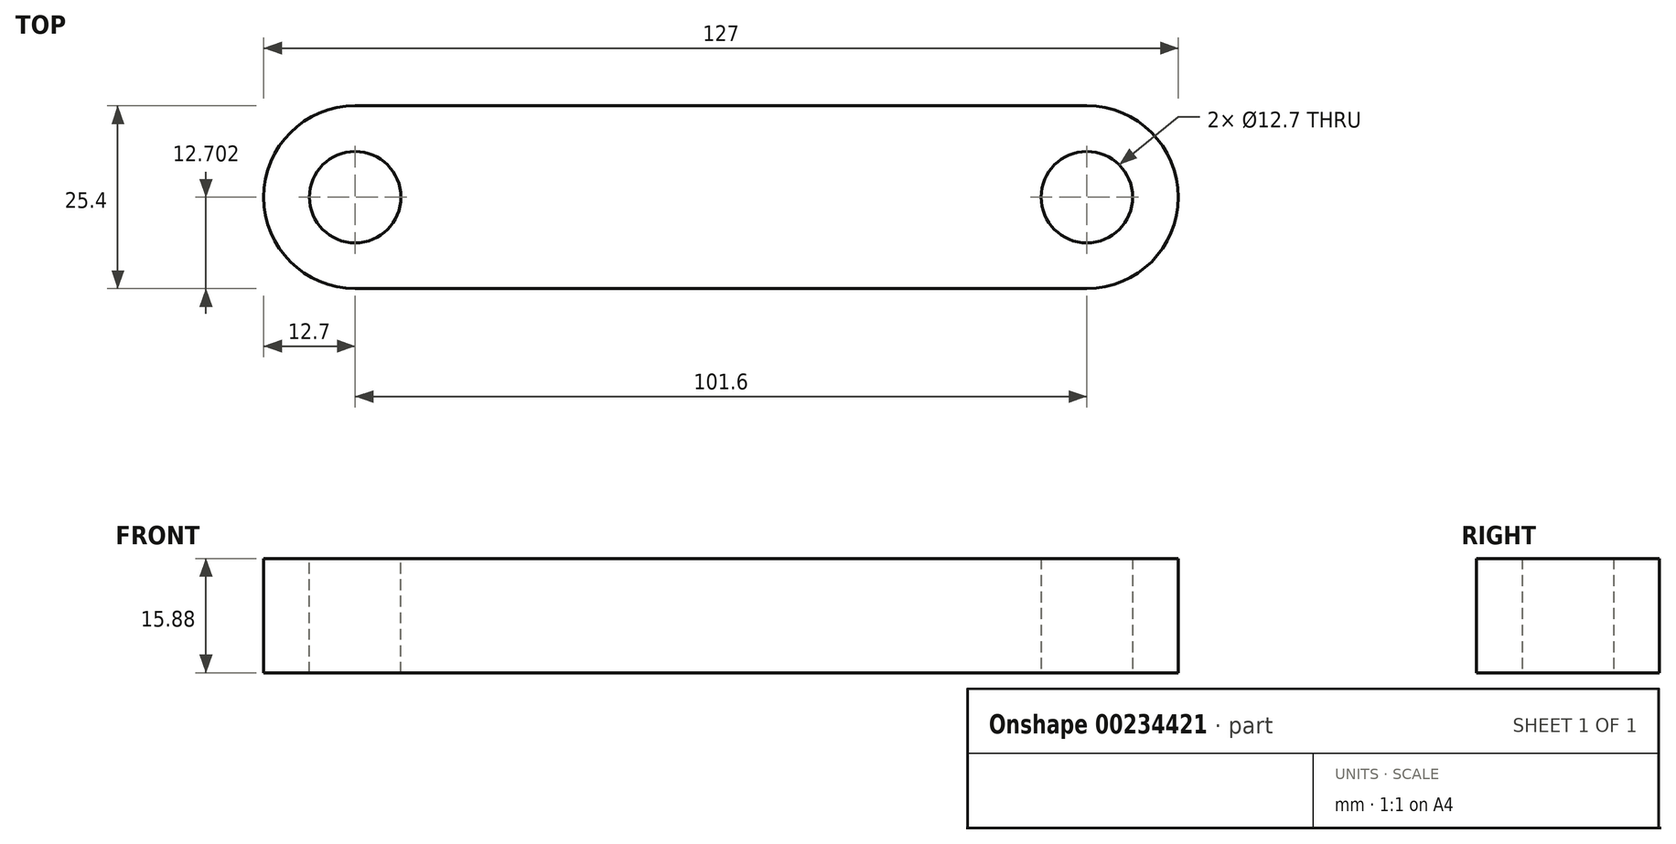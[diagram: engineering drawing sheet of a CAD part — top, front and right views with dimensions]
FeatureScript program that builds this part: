
annotation { "Feature Type Name" : "Feature", "Feature Type Description" : "" }
export const myFeature = defineFeature(function(context is Context, id is Id, definition is map)
    precondition{}
    {
        {
            var Q0;
            Q0=qCreatedBy(makeId("Top.planeOp"),FACE);
            var sketch = newSketch(context, id + "F0", { "sketchPlane" : qUnion([Q0])});
            skLineSegment(sketch, "E0.bottom", {"start": v(1.78, -0.58) * mm, "end": v(128.78, -0.58) * mm});
            skLineSegment(sketch, "E0.top", {"start": v(1.78, 24.82) * mm, "end": v(128.78, 24.82) * mm});
            skLineSegment(sketch, "E0.left", {"start": v(1.78, -0.58) * mm, "end": v(1.78, 24.82) * mm});
            skLineSegment(sketch, "E0.right", {"start": v(128.78, -0.58) * mm, "end": v(128.78, 24.82) * mm});
            skSolve(sketch);
        }
        {
            var Q0;
            Q0=makeQuery(id+"F0.imprint","IMPRINT",FACE,{"disambiguationData":[TD([[makeQuery(id+"F0.imprint","IMPRINT",EDGE,{"derivedFrom":sQuery(id+"F0.wireOp",EDGE,"E0.bottom")}),1.0]])]});
            extrude(context, id + "F1", {"entities" : qUnion([Q0]), "depth" : 15.88 * mm});
        }
        {
            var Q0;
            Q0=makeQuery(id+"F1.opExtrude","CAP_FACE",FACE,{"disambiguationData":[OSD([sQuery(id+"F0.wireOp",EDGE,"E0.bottom"),sQuery(id+"F0.wireOp",EDGE,"E0.top"),sQuery(id+"F0.wireOp",EDGE,"E0.left"),sQuery(id+"F0.wireOp",EDGE,"E0.right")])],"isStart":true});
            var sketch = newSketch(context, id + "F2", { "sketchPlane" : qUnion([Q0])});
            skCircle(sketch, "E1", {"center": v(116.08, -12.12) * mm, "radius": 6.35 * mm});
            skSolve(sketch);
        }
        {
            var Q0;
            Q0=makeQuery(id+"F2.imprint","IMPRINT",FACE,{"disambiguationData":[TD([[makeQuery(id+"F2.imprint","IMPRINT",EDGE,{"derivedFrom":sQuery(id+"F2.wireOp",EDGE,"E1")}),1.0]])]});
            extrude(context, id + "F3", {"entities" : qUnion([Q0]), "operationType" : NewBodyOperationType.REMOVE, "endBound" : BoundingType.THROUGH_ALL, "oppositeDirection" : true, "depth" : 25.4 * mm});
        }
        {
            var Q0;
            Q0=makeQuery(id+"F1.opExtrude","SWEPT_EDGE",EDGE,{"disambiguationData":[OSD([sQuery(id+"F0.wireOp",EDGE,"E0.top"),sQuery(id+"F0.wireOp",EDGE,"E0.right")])]});
            var Q1;
            Q1=makeQuery(id+"F1.opExtrude","SWEPT_EDGE",EDGE,{"disambiguationData":[OSD([sQuery(id+"F0.wireOp",EDGE,"E0.bottom"),sQuery(id+"F0.wireOp",EDGE,"E0.right")])]});
            fillet(context, id + "F4", {"entities" : qUnion([Q0, Q1]), "radius" : 12.7 * mm, "tangentPropagation" : true, "allowEdgeOverflow" : false});
        }
        {
            var Q0;
            Q0=makeQuery(id+"F1.opExtrude","CAP_FACE",FACE,{"disambiguationData":[OSD([sQuery(id+"F0.wireOp",EDGE,"E0.bottom"),sQuery(id+"F0.wireOp",EDGE,"E0.top"),sQuery(id+"F0.wireOp",EDGE,"E0.left"),sQuery(id+"F0.wireOp",EDGE,"E0.right")])],"isStart":false});
            var sketch = newSketch(context, id + "F5", { "sketchPlane" : qUnion([Q0])});
            skCircle(sketch, "E2", {"center": v(14.48, 12.12) * mm, "radius": 6.35 * mm});
            skSolve(sketch);
        }
        {
            var Q0;
            Q0=makeQuery(id+"F5.imprint","IMPRINT",FACE,{"disambiguationData":[TD([[makeQuery(id+"F5.imprint","IMPRINT",EDGE,{"derivedFrom":sQuery(id+"F5.wireOp",EDGE,"E2")}),1.0]])]});
            var Q1;
            Q1=sQuery(id+"F5.wireOp",EDGE,"E2");
            extrude(context, id + "F6", {"entities" : qUnion([Q0]), "operationType" : NewBodyOperationType.REMOVE, "surfaceEntities" : qUnion([Q1]), "endBound" : BoundingType.THROUGH_ALL, "oppositeDirection" : true, "depth" : 25.4 * mm});
        }
        {
            var Q0;
            Q0=makeQuery(id+"F1.opExtrude","SWEPT_EDGE",EDGE,{"disambiguationData":[OSD([sQuery(id+"F0.wireOp",EDGE,"E0.top"),sQuery(id+"F0.wireOp",EDGE,"E0.left")])]});
            var Q1;
            Q1=makeQuery(id+"F1.opExtrude","SWEPT_EDGE",EDGE,{"disambiguationData":[OSD([sQuery(id+"F0.wireOp",EDGE,"E0.bottom"),sQuery(id+"F0.wireOp",EDGE,"E0.left")])]});
            fillet(context, id + "F7", {"entities" : qUnion([Q0, Q1]), "radius" : 12.7 * mm, "tangentPropagation" : true, "allowEdgeOverflow" : false});
        }
    });
